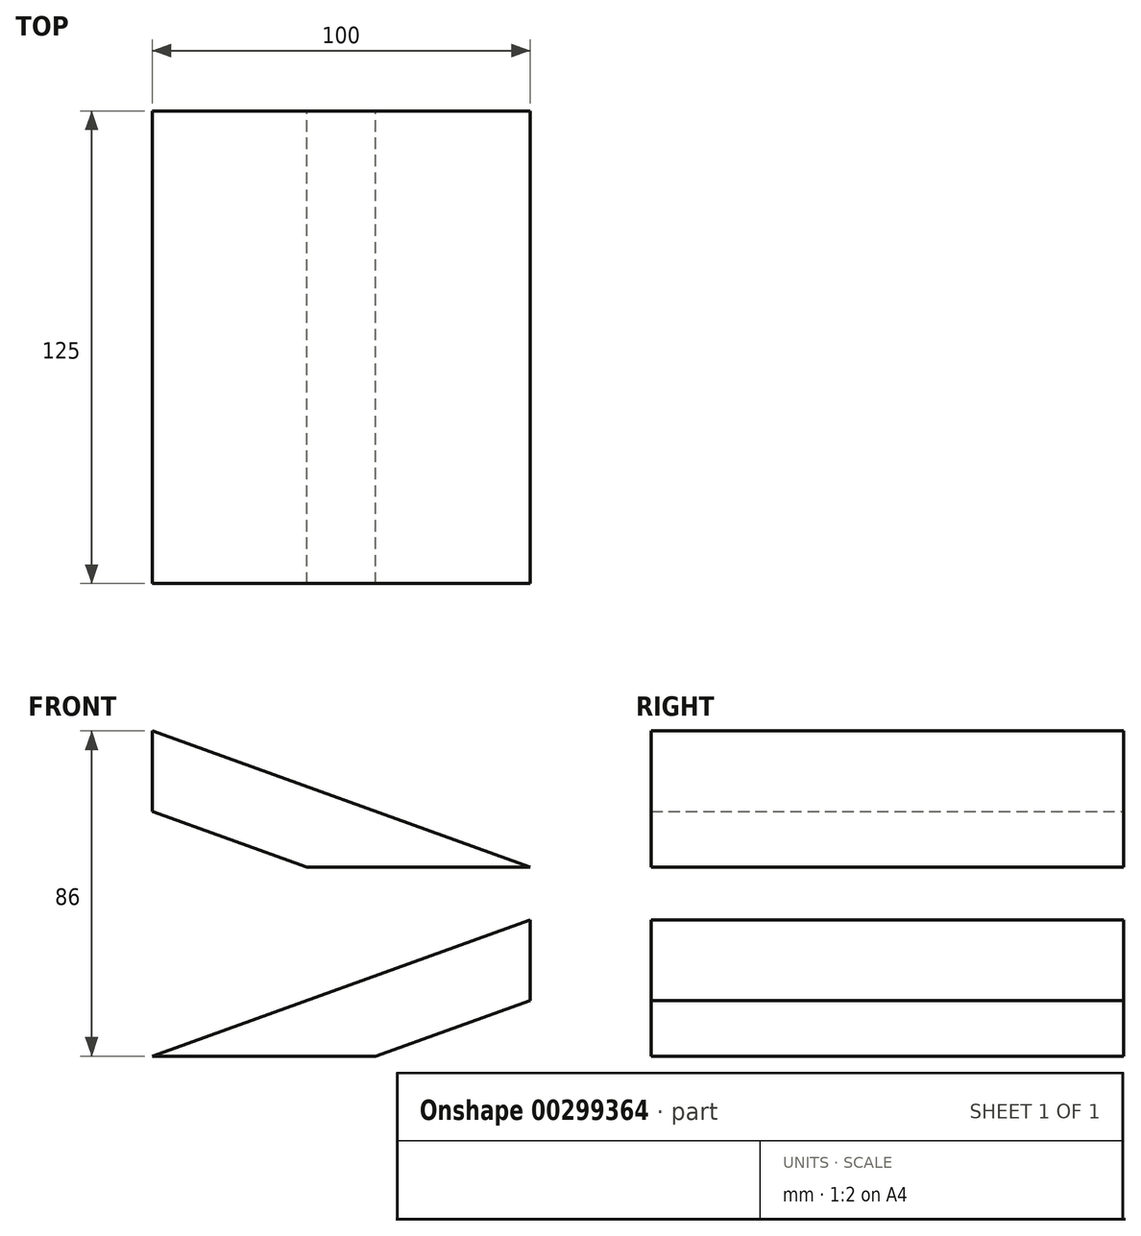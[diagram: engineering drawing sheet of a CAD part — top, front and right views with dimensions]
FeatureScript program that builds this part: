
annotation { "Feature Type Name" : "Feature", "Feature Type Description" : "" }
export const myFeature = defineFeature(function(context is Context, id is Id, definition is map)
    precondition{}
    {
        {
            var Q0;
            Q0=qCreatedBy(makeId("Front.planeOp"),FACE);
            var sketch = newSketch(context, id + "F0", { "sketchPlane" : qUnion([Q0])});
            skLineSegment(sketch, "E0", {"start": v(-45.1, -27.39) * mm, "end": v(54.9, 8.61) * mm});
            skLineSegment(sketch, "E1", {"start": v(54.9, -12.64) * mm, "end": v(54.9, 8.61) * mm});
            skLineSegment(sketch, "E2", {"start": v(-45.1, -27.39) * mm, "end": v(54.9, -27.39) * mm});
            skLineSegment(sketch, "E3", {"start": v(54.9, -27.39) * mm, "end": v(54.9, 8.61) * mm});
            skLineSegment(sketch, "E4", {"start": v(54.9, 8.61) * mm, "end": v(54.9, 22.61) * mm});
            skLineSegment(sketch, "E5", {"start": v(54.9, 22.61) * mm, "end": v(-45.1, 22.61) * mm});
            skLineSegment(sketch, "E6", {"start": v(-45.1, 22.61) * mm, "end": v(-45.1, 58.61) * mm});
            skLineSegment(sketch, "E7", {"start": v(-45.1, 58.61) * mm, "end": v(54.9, 22.61) * mm});
            skLineSegment(sketch, "E8", {"start": v(-45.1, -27.39) * mm, "end": v(13.94, -27.39) * mm});
            skLineSegment(sketch, "E9", {"start": v(13.94, -27.39) * mm, "end": v(54.9, -12.64) * mm});
            skLineSegment(sketch, "E10", {"start": v(-45.1, 37.36) * mm, "end": v(-4.15, 22.61) * mm});
            skSolve(sketch);
        }
        {
            var Q0;
            {var subQ0=sQuery(id+"F0.wireOp",EDGE,"E0");Q0=makeQuery(id+"F0.imprint","IMPRINT",FACE,{"disambiguationData":[TD([[makeQuery(id+"F0.imprint","IMPRINT",EDGE,{"derivedFrom":subQ0}),-1.0]])]});}
            var Q1;
            {var subQ0=sQuery(id+"F0.wireOp",EDGE,"E7");Q1=makeQuery(id+"F0.imprint","IMPRINT",FACE,{"disambiguationData":[TD([[makeQuery(id+"F0.imprint","IMPRINT",EDGE,{"derivedFrom":subQ0}),-1.0]])]});}
            extrude(context, id + "F1", {"entities" : qUnion([Q0, Q1]), "endBound" : BoundingType.SYMMETRIC, "offsetDistance" : 25 * mm, "depth" : 125 * mm});
        }
    });
